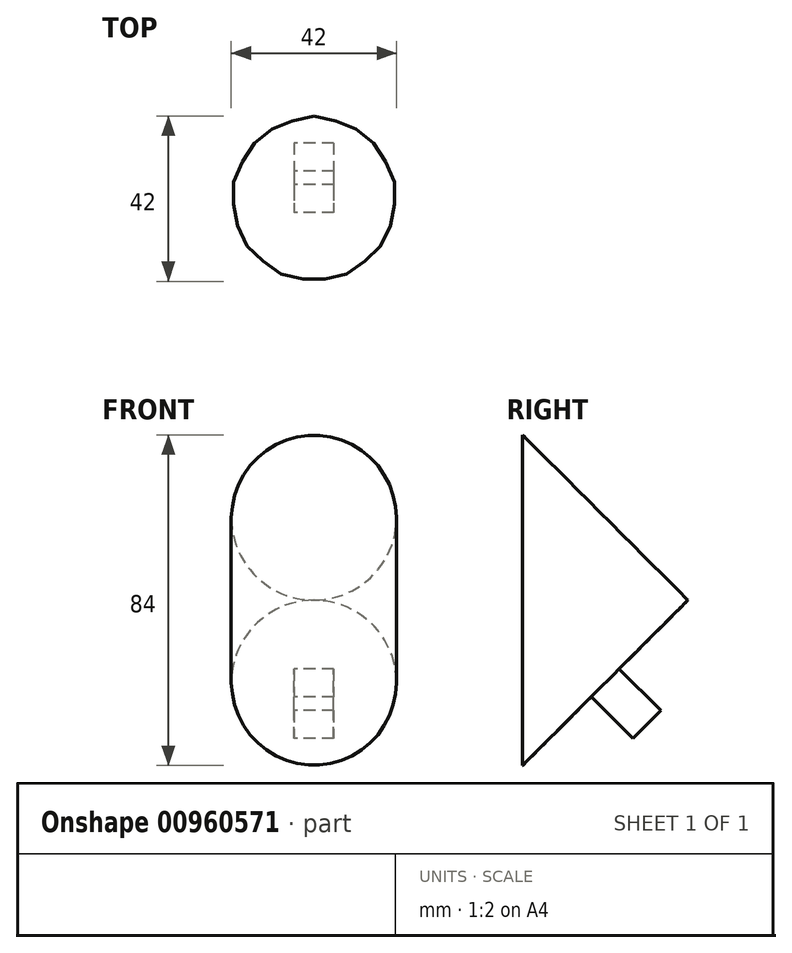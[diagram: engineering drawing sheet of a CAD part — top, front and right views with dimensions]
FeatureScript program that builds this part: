
annotation { "Feature Type Name" : "Feature", "Feature Type Description" : "" }
export const myFeature = defineFeature(function(context is Context, id is Id, definition is map)
    precondition{}
    {
        {
            var Q0;
            Q0=qCreatedBy(makeId("Top.planeOp"),FACE);
            var sketch = newSketch(context, id + "F0", { "sketchPlane" : qUnion([Q0])});
            skCircle(sketch, "E0", {"center": v(0, 0) * mm, "radius": 21 * mm});
            skSolve(sketch);
        }
        {
            var Q0;
            Q0=qCreatedBy(makeId("Right.planeOp"),FACE);
            var sketch = newSketch(context, id + "F1", { "sketchPlane" : qUnion([Q0])});
            skLineSegment(sketch, "E1.bottom", {"start": v(21, 50) * mm, "end": v(-21, 50) * mm});
            skLineSegment(sketch, "E1.top", {"start": v(21, -50) * mm, "end": v(-21, -50) * mm});
            skLineSegment(sketch, "E1.left", {"start": v(21, 50) * mm, "end": v(21, -50) * mm});
            skLineSegment(sketch, "E1.right", {"start": v(-21, 50) * mm, "end": v(-21, -50) * mm});
            skPoint(sketch, "E1.middle", {"position": v(0, 0) * mm});
            skLineSegment(sketch, "E2", {"start": v(-21, 50) * mm, "end": v(21, 8) * mm});
            skLineSegment(sketch, "E3", {"start": v(21, 8) * mm, "end": v(-21, -34) * mm});
            skSolve(sketch);
        }
        {
            var Q0;
            Q0 = qSketchRegion(id + "F0", true);
            extrude(context, id + "F2", {"entities" : qUnion([Q0]), "depth" : 100 * mm, "offsetDistance" : 25 * mm, "symmetric" : true});
        }
        {
            var Q0;
            {var subQ0=sQuery(id+"F1.wireOp",EDGE,"E1.bottom");Q0=makeQuery(id+"F1.imprint","IMPRINT",FACE,{"disambiguationData":[TD([[makeQuery(id+"F1.imprint","IMPRINT",EDGE,{"derivedFrom":subQ0}),1.0]])]});}
            var Q1;
            {var subQ0=sQuery(id+"F1.wireOp",EDGE,"E1.top");Q1=makeQuery(id+"F1.imprint","IMPRINT",FACE,{"disambiguationData":[TD([[makeQuery(id+"F1.imprint","IMPRINT",EDGE,{"derivedFrom":subQ0}),-1.0]])]});}
            extrude(context, id + "F3", {"entities" : qUnion([Q0, Q1]), "operationType" : NewBodyOperationType.REMOVE, "oppositeDirection" : true, "depth" : 42 * mm, "offsetDistance" : 25 * mm, "symmetric" : true});
        }
        {
            var Q0;
            Q0=makeQuery(id+"F3.boolean.opBoolean","COPY",FACE,{"derivedFrom":makeQuery(id+"F3.opExtrude","SWEPT_FACE",FACE,{"disambiguationData":[OSD([sQuery(id+"F1.wireOp",EDGE,"E3")])]})});
            var sketch = newSketch(context, id + "F4", { "sketchPlane" : qUnion([Q0])});
            skLineSegment(sketch, "E4.bottom", {"start": v(-5, -4.2) * mm, "end": v(5, -4.2) * mm});
            skLineSegment(sketch, "E4.top", {"start": v(-5, -14.2) * mm, "end": v(5, -14.2) * mm});
            skLineSegment(sketch, "E4.left", {"start": v(-5, -4.2) * mm, "end": v(-5, -14.2) * mm});
            skLineSegment(sketch, "E4.right", {"start": v(5, -4.2) * mm, "end": v(5, -14.2) * mm});
            skPoint(sketch, "E4.middle", {"position": v(0, -9.2) * mm});
            skSolve(sketch);
        }
        {
            var Q0;
            Q0 = qSketchRegion(id + "F4", true);
            extrude(context, id + "F5", {"entities" : qUnion([Q0]), "operationType" : NewBodyOperationType.ADD, "depth" : 15 * mm, "offsetDistance" : 25 * mm});
        }
    });
